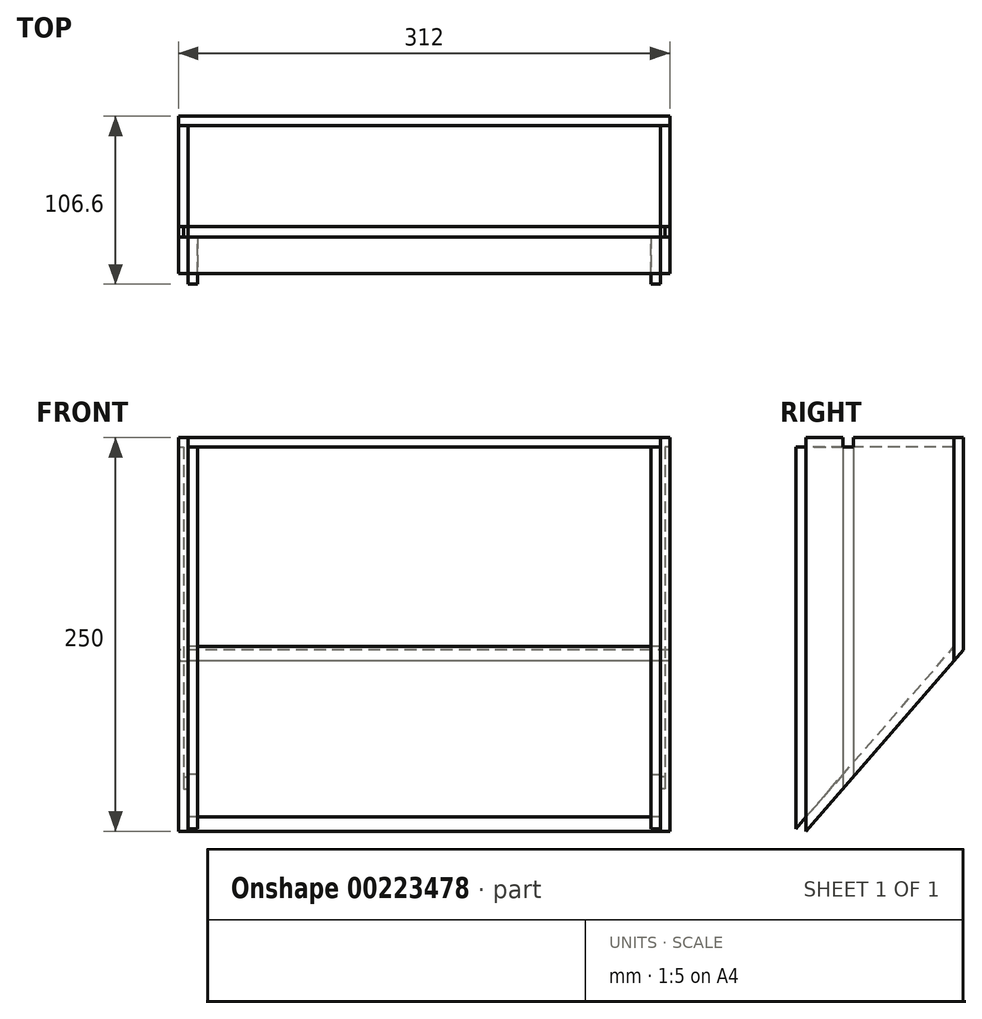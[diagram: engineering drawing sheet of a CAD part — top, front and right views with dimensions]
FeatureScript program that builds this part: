
annotation { "Feature Type Name" : "Feature", "Feature Type Description" : "" }
export const myFeature = defineFeature(function(context is Context, id is Id, definition is map)
    precondition{}
    {
        {
            var Q0;
            Q0=qCreatedBy(makeId("Front.planeOp"),FACE);
            var sketch = newSketch(context, id + "F0", { "sketchPlane" : qUnion([Q0])});
            skLineSegment(sketch, "E0.bottom", {"start": v(150, 150) * mm, "end": v(-150, 150) * mm});
            skLineSegment(sketch, "E0.top", {"start": v(150, -150) * mm, "end": v(-150, -150) * mm});
            skLineSegment(sketch, "E0.left", {"start": v(150, 150) * mm, "end": v(150, -150) * mm});
            skLineSegment(sketch, "E0.right", {"start": v(-150, 150) * mm, "end": v(-150, -150) * mm});
            skPoint(sketch, "E0.middle", {"position": v(0, 0) * mm});
            skLineSegment(sketch, "E1", {"start": v(-292.39, -200) * mm, "end": v(238.39, -200) * mm, "construction": true});
            skLineSegment(sketch, "E2", {"start": v(-292.39, -180) * mm, "end": v(238.39, -180) * mm, "construction": true});
            skSolve(sketch);
        }
        {
            var Q0;
            Q0=qCreatedBy(makeId("Right.planeOp"),FACE);
            var Q1;
            Q1=sQuery(id+"F0.wireOp",VERTEX,"E0.right.start");
            cPlane(context, id + "F1", {"entities" : qUnion([Q0, Q1]), "cplaneType" : CPlaneType.PLANE_POINT, "offset" : 25 * mm, "width" : 150 * mm, "height" : 150 * mm});
        }
        {
            var Q0;
            Q0=qCreatedBy(id+"F1.planeOp",FACE);
            var sketch = newSketch(context, id + "F2", { "sketchPlane" : qUnion([Q0])});
            skLineSegment(sketch, "E3", {"start": v(0, 150) * mm, "end": v(100.6, 150) * mm});
            skLineSegment(sketch, "E4", {"start": v(100.6, 156) * mm, "end": v(100.6, 14.13) * mm});
            skLineSegment(sketch, "E5", {"start": v(100.6, 23.28) * mm, "end": v(0, -92.45) * mm});
            skLineSegment(sketch, "E6.0", {"start": v(0, 150) * mm, "end": v(0, -150) * mm});
            skLineSegment(sketch, "E7.bottom", {"start": v(0, 150) * mm, "end": v(6.6, 150) * mm, "construction": true});
            skLineSegment(sketch, "E7.top", {"start": v(0, -92.45) * mm, "end": v(6.6, -92.45) * mm, "construction": true});
            skLineSegment(sketch, "E7.left", {"start": v(0, 150) * mm, "end": v(0, -92.45) * mm, "construction": true});
            skLineSegment(sketch, "E7.right", {"start": v(6.6, 150) * mm, "end": v(6.6, -92.45) * mm});
            skLineSegment(sketch, "E8.0", {"start": v(106.6, 21.04) * mm, "end": v(6.6, -94) * mm});
            skLineSegment(sketch, "E8.1", {"start": v(106.6, 156) * mm, "end": v(106.6, 21.04) * mm});
            skLineSegment(sketch, "E8.2", {"start": v(6.6, 156) * mm, "end": v(106.6, 156) * mm});
            skLineSegment(sketch, "E9", {"start": v(6.6, 150) * mm, "end": v(6.6, 156) * mm});
            skLineSegment(sketch, "E10", {"start": v(6.6, -84.85) * mm, "end": v(6.6, -94) * mm});
            skPoint(sketch, "E11.oppositeSnap0", {"position": v(56.6, 156) * mm});
            skLineSegment(sketch, "E11.bottom", {"start": v(36.5, 156) * mm, "end": v(30, 156) * mm});
            skLineSegment(sketch, "E11.left", {"start": v(36.5, 156) * mm, "end": v(36.5, -59.6) * mm});
            skLineSegment(sketch, "E11.right", {"start": v(30, 156) * mm, "end": v(30, -67.08) * mm});
            skLineSegment(sketch, "E12", {"start": v(30, 144) * mm, "end": v(0, 144) * mm});
            skLineSegment(sketch, "E13", {"start": v(30, -48.8) * mm, "end": v(0, -83.3) * mm});
            skSolve(sketch);
        }
        {
            var Q0;
            {var subQ0=sQuery(id+"F2.wireOp",EDGE,"E4");Q0=makeQuery(id+"F2.imprint","IMPRINT",FACE,{"disambiguationData":[TD([[makeQuery(id+"F2.imprint","IMPRINT",EDGE,{"derivedFrom":subQ0}),-1.0]])]});}
            var Q1;
            {var subQ0=sQuery(id+"F2.wireOp",EDGE,"E9");Q1=makeQuery(id+"F2.imprint","IMPRINT",FACE,{"disambiguationData":[TD([[makeQuery(id+"F2.imprint","IMPRINT",EDGE,{"derivedFrom":subQ0}),-1.0]])]});}
            var Q2;
            {var subQ0=sQuery(id+"F2.wireOp",EDGE,"E11.right");var subQ2=sQuery(id+"F2.wireOp",EDGE,"E3");var subQ3=makeQuery(id+"F2.imprint","INTERSECT",VERTEX,{"derivedFrom":[subQ2,subQ0]});Q2=makeQuery(id+"F2.imprint","IMPRINT",FACE,{"disambiguationData":[TD([[makeQuery(id+"F2.imprint","IMPRINT",EDGE,{"disambiguationData":[TD([[subQ3,-1.0]])],"derivedFrom":subQ2}),-1.0]])]});}
            var Q3;
            {var subQ5=sQuery(id+"F2.wireOp",EDGE,"E11.bottom");Q3=makeQuery(id+"F2.imprint","IMPRINT",FACE,{"disambiguationData":[TD([[makeQuery(id+"F2.imprint","IMPRINT",EDGE,{"derivedFrom":subQ5}),1.0]])]});}
            var Q4;
            {var subQ0=sQuery(id+"F2.wireOp",EDGE,"E11.left");var subQ1=sQuery(id+"F2.wireOp",EDGE,"E5");var subQ2=makeQuery(id+"F2.imprint","INTERSECT",VERTEX,{"derivedFrom":[subQ1,subQ0]});Q4=makeQuery(id+"F2.imprint","IMPRINT",FACE,{"disambiguationData":[TD([[makeQuery(id+"F2.imprint","IMPRINT",EDGE,{"disambiguationData":[TD([[subQ2,-1.0]])],"derivedFrom":subQ1}),1.0]])]});}
            var Q5;
            {var subQ0=sQuery(id+"F2.wireOp",EDGE,"E10");Q5=makeQuery(id+"F2.imprint","IMPRINT",FACE,{"disambiguationData":[TD([[makeQuery(id+"F2.imprint","IMPRINT",EDGE,{"derivedFrom":subQ0}),1.0]])]});}
            var Q6;
            {var subQ0=sQuery(id+"F2.wireOp",EDGE,"E12");var subQ1=sQuery(id+"F2.wireOp",EDGE,"E7.right");var subQ2=makeQuery(id+"F2.imprint","INTERSECT",VERTEX,{"derivedFrom":[subQ1,subQ0]});Q6=makeQuery(id+"F2.imprint","IMPRINT",FACE,{"disambiguationData":[TD([[makeQuery(id+"F2.imprint","IMPRINT",EDGE,{"disambiguationData":[TD([[subQ2,-1.0]])],"derivedFrom":subQ1}),1.0]])]});}
            var Q7;
            {var subQ3=sQuery(id+"F2.wireOp",EDGE,"E11.right");var subQ5=sQuery(id+"F2.wireOp",EDGE,"E12");var subQ6=makeQuery(id+"F2.imprint","INTERSECT",VERTEX,{"derivedFrom":[subQ3,subQ5]});Q7=makeQuery(id+"F2.imprint","IMPRINT",FACE,{"disambiguationData":[TD([[makeQuery(id+"F2.imprint","IMPRINT",EDGE,{"disambiguationData":[TD([[subQ6,1.0]])],"derivedFrom":subQ3}),-1.0]])]});}
            var Q8;
            {var subQ3=sQuery(id+"F2.wireOp",EDGE,"E11.right");var subQ5=sQuery(id+"F2.wireOp",EDGE,"E13");var subQ7=makeQuery(id+"F2.imprint","INTERSECT",VERTEX,{"derivedFrom":[subQ3,subQ5]});Q8=makeQuery(id+"F2.imprint","IMPRINT",FACE,{"disambiguationData":[TD([[makeQuery(id+"F2.imprint","IMPRINT",EDGE,{"disambiguationData":[TD([[subQ7,-1.0]])],"derivedFrom":subQ3}),-1.0]])]});}
            extrude(context, id + "F3", {"entities" : qUnion([Q0, Q1, Q2, Q3, Q4, Q5, Q6, Q7, Q8]), "oppositeDirection" : true, "depth" : 6 * mm});
        }
        {
            var Q0;
            {var subQ1=sQuery(id+"F2.wireOp",EDGE,"E3");var subQ5=sQuery(id+"F2.wireOp",EDGE,"E11.right");var subQ7=makeQuery(id+"F2.imprint","INTERSECT",VERTEX,{"derivedFrom":[subQ1,subQ5]});Q0=makeQuery(id+"F2.imprint","IMPRINT",FACE,{"disambiguationData":[TD([[makeQuery(id+"F2.imprint","IMPRINT",EDGE,{"disambiguationData":[TD([[subQ7,-1.0]])],"derivedFrom":subQ1}),-1.0]])]});}
            var Q1;
            {var subQ5=sQuery(id+"F2.wireOp",EDGE,"E11.bottom");Q1=makeQuery(id+"F2.imprint","IMPRINT",FACE,{"disambiguationData":[TD([[makeQuery(id+"F2.imprint","IMPRINT",EDGE,{"derivedFrom":subQ5}),1.0]])]});}
            var Q2;
            {var subQ0=sQuery(id+"F2.wireOp",EDGE,"E11.left");var subQ1=sQuery(id+"F2.wireOp",EDGE,"E5");var subQ2=makeQuery(id+"F2.imprint","INTERSECT",VERTEX,{"derivedFrom":[subQ1,subQ0]});Q2=makeQuery(id+"F2.imprint","IMPRINT",FACE,{"disambiguationData":[TD([[makeQuery(id+"F2.imprint","IMPRINT",EDGE,{"disambiguationData":[TD([[subQ2,-1.0]])],"derivedFrom":subQ1}),1.0]])]});}
            extrude(context, id + "F4", {"entities" : qUnion([Q0, Q1, Q2]), "operationType" : NewBodyOperationType.REMOVE, "oppositeDirection" : true, "depth" : 3 * mm});
        }
        {
            var Q0;
            {var subQ0=sQuery(id+"F2.wireOp",EDGE,"E12");var subQ1=sQuery(id+"F2.wireOp",EDGE,"E6.0");var subQ2=makeQuery(id+"F2.imprint","INTERSECT",VERTEX,{"derivedFrom":[subQ1,subQ0]});Q0=makeQuery(id+"F2.imprint","IMPRINT",FACE,{"disambiguationData":[TD([[makeQuery(id+"F2.imprint","IMPRINT",EDGE,{"disambiguationData":[TD([[subQ2,-1.0]])],"derivedFrom":subQ1}),1.0]])]});}
            var Q1;
            {var subQ0=sQuery(id+"F2.wireOp",EDGE,"E6.0");var subQ1=sQuery(id+"F2.wireOp",EDGE,"E3");var subQ2=makeQuery(id+"F2.imprint","INTERSECT",VERTEX,{"derivedFrom":[subQ1,subQ0]});Q1=makeQuery(id+"F2.imprint","IMPRINT",FACE,{"disambiguationData":[TD([[makeQuery(id+"F2.imprint","IMPRINT",EDGE,{"disambiguationData":[TD([[subQ2,-1.0]])],"derivedFrom":subQ0}),1.0]])]});}
            var Q2;
            {var subQ3=sQuery(id+"F2.wireOp",EDGE,"E11.right");var subQ5=sQuery(id+"F2.wireOp",EDGE,"E12");var subQ6=makeQuery(id+"F2.imprint","INTERSECT",VERTEX,{"derivedFrom":[subQ3,subQ5]});Q2=makeQuery(id+"F2.imprint","IMPRINT",FACE,{"disambiguationData":[TD([[makeQuery(id+"F2.imprint","IMPRINT",EDGE,{"disambiguationData":[TD([[subQ6,1.0]])],"derivedFrom":subQ3}),-1.0]])]});}
            var Q3;
            {var subQ0=sQuery(id+"F2.wireOp",EDGE,"E12");var subQ1=sQuery(id+"F2.wireOp",EDGE,"E7.right");var subQ2=makeQuery(id+"F2.imprint","INTERSECT",VERTEX,{"derivedFrom":[subQ1,subQ0]});Q3=makeQuery(id+"F2.imprint","IMPRINT",FACE,{"disambiguationData":[TD([[makeQuery(id+"F2.imprint","IMPRINT",EDGE,{"disambiguationData":[TD([[subQ2,-1.0]])],"derivedFrom":subQ1}),1.0]])]});}
            var Q4;
            {var subQ3=sQuery(id+"F2.wireOp",EDGE,"E11.right");var subQ5=sQuery(id+"F2.wireOp",EDGE,"E13");var subQ7=makeQuery(id+"F2.imprint","INTERSECT",VERTEX,{"derivedFrom":[subQ3,subQ5]});Q4=makeQuery(id+"F2.imprint","IMPRINT",FACE,{"disambiguationData":[TD([[makeQuery(id+"F2.imprint","IMPRINT",EDGE,{"disambiguationData":[TD([[subQ7,-1.0]])],"derivedFrom":subQ3}),-1.0]])]});}
            var Q5;
            {var subQ0=sQuery(id+"F2.wireOp",EDGE,"E6.0");var subQ1=sQuery(id+"F2.wireOp",EDGE,"E5");var subQ2=makeQuery(id+"F2.imprint","INTERSECT",VERTEX,{"derivedFrom":[subQ1,subQ0]});Q5=makeQuery(id+"F2.imprint","IMPRINT",FACE,{"disambiguationData":[TD([[makeQuery(id+"F2.imprint","IMPRINT",EDGE,{"disambiguationData":[TD([[subQ2,1.0]])],"derivedFrom":subQ0}),1.0]])]});}
            extrude(context, id + "F5", {"entities" : qUnion([Q0, Q1, Q2, Q3, Q4, Q5]), "depth" : 6 * mm});
        }
        {
            var Q0;
            Q0=makeQuery(id+"F3.opExtrude","SWEPT_BODY",BODY,{"disambiguationData":[OSD([sQuery(id+"F2.wireOp",EDGE,"E7.right"),sQuery(id+"F2.wireOp",EDGE,"E8.0"),sQuery(id+"F2.wireOp",EDGE,"E8.1"),sQuery(id+"F2.wireOp",EDGE,"E8.2"),sQuery(id+"F2.wireOp",EDGE,"E9"),sQuery(id+"F2.wireOp",EDGE,"E10"),sQuery(id+"F2.wireOp",EDGE,"E11.bottom")])]});
            var Q1;
            Q1=makeQuery(id+"F5.opExtrude","SWEPT_BODY",BODY,{"disambiguationData":[OSD([sQuery(id+"F2.wireOp",EDGE,"E3"),sQuery(id+"F2.wireOp",EDGE,"E5"),sQuery(id+"F2.wireOp",EDGE,"E6.0"),sQuery(id+"F2.wireOp",EDGE,"E11.right")])]});
            var Q2;
            Q2=qCreatedBy(makeId("Right.planeOp"),FACE);
            mirror(context, id + "F6", {"entities" : qUnion([Q0, Q1]), "mirrorPlane" : qUnion([Q2])});
        }
        {
            var Q0;
            {var subQ3=sQuery(id+"F2.wireOp",EDGE,"E8.1");Q0=makeQuery(id+"F2.imprint","IMPRINT",FACE,{"disambiguationData":[TD([[makeQuery(id+"F2.imprint","IMPRINT",EDGE,{"derivedFrom":subQ3}),-1.0]])]});}
            var Q1;
            Q1=makeQuery(id+"F6.opPattern","COPY",FACE,{"derivedFrom":makeQuery(id+"F3.opExtrude","CAP_FACE",FACE,{"disambiguationData":[OSD([sQuery(id+"F2.wireOp",EDGE,"E4"),sQuery(id+"F2.wireOp",EDGE,"E7.right"),sQuery(id+"F2.wireOp",EDGE,"E8.0"),sQuery(id+"F2.wireOp",EDGE,"E8.2"),sQuery(id+"F2.wireOp",EDGE,"E9"),sQuery(id+"F2.wireOp",EDGE,"E10"),sQuery(id+"F2.wireOp",EDGE,"E11.bottom")])],"isStart":false}),"instanceName":"1"});
            var Q2;
            Q2=makeQuery(id+"F3.opExtrude","CAP_FACE",FACE,{"disambiguationData":[OSD([sQuery(id+"F2.wireOp",EDGE,"E4"),sQuery(id+"F2.wireOp",EDGE,"E7.right"),sQuery(id+"F2.wireOp",EDGE,"E8.0"),sQuery(id+"F2.wireOp",EDGE,"E8.2"),sQuery(id+"F2.wireOp",EDGE,"E9"),sQuery(id+"F2.wireOp",EDGE,"E10"),sQuery(id+"F2.wireOp",EDGE,"E11.bottom")])],"isStart":false});
            extrude(context, id + "F7", {"entities" : qUnion([Q0]), "endBound" : BoundingType.UP_TO_SURFACE, "endBoundEntityFace" : qUnion([Q1]), "depth" : 25 * mm, "hasSecondDirection" : true, "secondDirectionBound" : SecondDirectionBoundingType.UP_TO_SURFACE, "secondDirectionOppositeDirection" : true, "secondDirectionBoundEntityFace" : qUnion([Q2]), "secondDirectionDepth" : 25 * mm});
        }
        {
            var Q0;
            {var subQ0=sQuery(id+"F2.wireOp",EDGE,"E8.0");var subQ1=sQuery(id+"F2.wireOp",EDGE,"E4");var subQ2=makeQuery(id+"F2.imprint","INTERSECT",VERTEX,{"derivedFrom":[subQ1,subQ0]});Q0=makeQuery(id+"F2.imprint","IMPRINT",FACE,{"disambiguationData":[TD([[makeQuery(id+"F2.imprint","IMPRINT",EDGE,{"disambiguationData":[TD([[subQ2,1.0]])],"derivedFrom":subQ1}),-1.0]])]});}
            var Q1;
            {var subQ0=sQuery(id+"F2.wireOp",EDGE,"E11.left");var subQ1=sQuery(id+"F2.wireOp",EDGE,"E5");var subQ2=makeQuery(id+"F2.imprint","INTERSECT",VERTEX,{"derivedFrom":[subQ1,subQ0]});Q1=makeQuery(id+"F2.imprint","IMPRINT",FACE,{"disambiguationData":[TD([[makeQuery(id+"F2.imprint","IMPRINT",EDGE,{"disambiguationData":[TD([[subQ2,-1.0]])],"derivedFrom":subQ1}),1.0]])]});}
            var Q2;
            {var subQ0=sQuery(id+"F2.wireOp",EDGE,"E10");var subQ5=sQuery(id+"F2.wireOp",EDGE,"E8.0");var subQ6=makeQuery(id+"F2.imprint","INTERSECT",VERTEX,{"derivedFrom":[subQ5,subQ0]});Q2=makeQuery(id+"F2.imprint","IMPRINT",FACE,{"disambiguationData":[TD([[makeQuery(id+"F2.imprint","IMPRINT",EDGE,{"disambiguationData":[TD([[subQ6,1.0]])],"derivedFrom":subQ5}),-1.0]])]});}
            var Q3;
            {var subQ0=sQuery(id+"F2.wireOp",EDGE,"E9");Q3=makeQuery(id+"F2.imprint","IMPRINT",FACE,{"disambiguationData":[TD([[makeQuery(id+"F2.imprint","IMPRINT",EDGE,{"derivedFrom":subQ0}),-1.0]])]});}
            var Q4;
            {var subQ5=sQuery(id+"F2.wireOp",EDGE,"E11.bottom");Q4=makeQuery(id+"F2.imprint","IMPRINT",FACE,{"disambiguationData":[TD([[makeQuery(id+"F2.imprint","IMPRINT",EDGE,{"derivedFrom":subQ5}),1.0]])]});}
            var Q5;
            {var subQ0=sQuery(id+"F2.wireOp",EDGE,"E4");var subQ1=sQuery(id+"F2.wireOp",EDGE,"E3");var subQ2=makeQuery(id+"F2.imprint","INTERSECT",VERTEX,{"derivedFrom":[subQ1,subQ0]});Q5=makeQuery(id+"F2.imprint","IMPRINT",FACE,{"disambiguationData":[TD([[makeQuery(id+"F2.imprint","IMPRINT",EDGE,{"disambiguationData":[TD([[subQ2,1.0]])],"derivedFrom":subQ1}),1.0]])]});}
            var Q6;
            {var subQ0=sQuery(id+"F2.wireOp",EDGE,"E4");var subQ1=sQuery(id+"F2.wireOp",EDGE,"E8.0");var subQ2=sQuery(id+"F2.wireOp",EDGE,"E11.bottom");var subQ3=sQuery(id+"F2.wireOp",EDGE,"E8.2");Q6=makeQuery(id+"F6.opPattern","COPY",FACE,{"derivedFrom":makeQuery(id+"F4.boolean.opBoolean","SPLIT",FACE,{"disambiguationData":[TD([makeQuery(id+"F3.opExtrude","SWEPT_FACE",FACE,{"disambiguationData":[OSD([subQ0])]})])],"derivedFrom":makeQuery(id+"F3.opExtrude","CAP_FACE",FACE,{"disambiguationData":[OSD([subQ0,sQuery(id+"F2.wireOp",EDGE,"E7.right"),subQ1,subQ3,sQuery(id+"F2.wireOp",EDGE,"E9"),sQuery(id+"F2.wireOp",EDGE,"E10"),subQ2])],"isStart":true})}),"instanceName":"1"});}
            extrude(context, id + "F8", {"entities" : qUnion([Q0, Q1, Q2, Q3, Q4, Q5]), "endBound" : BoundingType.UP_TO_SURFACE, "endBoundEntityFace" : qUnion([Q6]), "depth" : 25 * mm});
        }
    });
